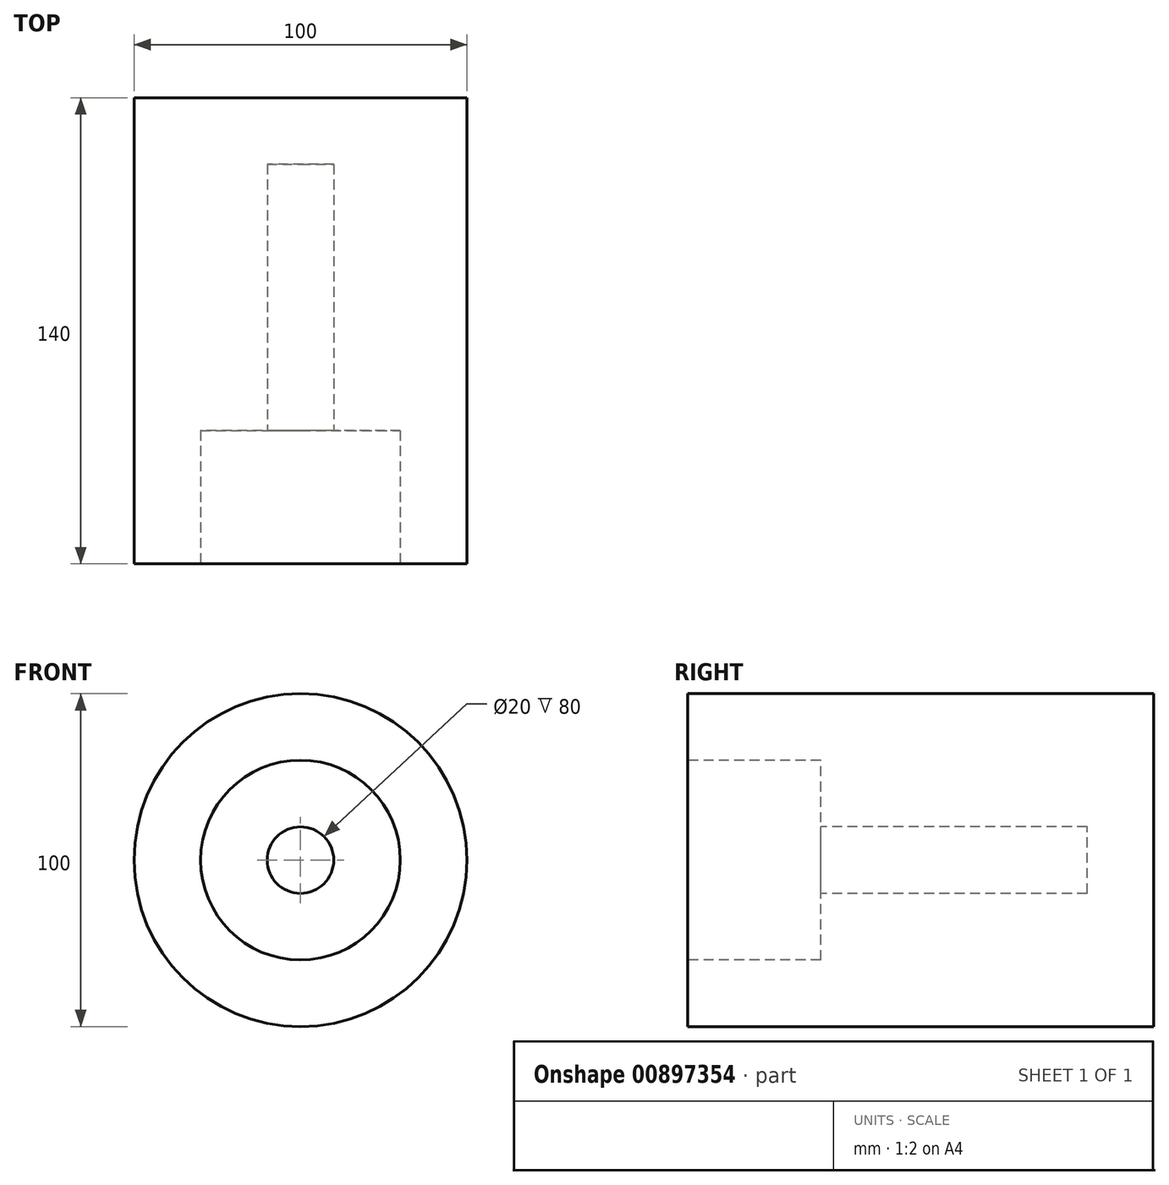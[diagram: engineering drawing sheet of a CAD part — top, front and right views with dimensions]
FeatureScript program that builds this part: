
annotation { "Feature Type Name" : "Feature", "Feature Type Description" : "" }
export const myFeature = defineFeature(function(context is Context, id is Id, definition is map)
    precondition{}
    {
        {
            var Q0;
            Q0=qCreatedBy(makeId("Front.planeOp"),FACE);
            var sketch = newSketch(context, id + "F0", { "sketchPlane" : qUnion([Q0])});
            skCircle(sketch, "E0", {"center": v(0, 0) * mm, "radius": 50 * mm});
            skSolve(sketch);
        }
        {
            var Q0;
            Q0=makeQuery(id+"F0.imprint","IMPRINT",FACE,{"disambiguationData":[TD([[makeQuery(id+"F0.imprint","IMPRINT",EDGE,{"derivedFrom":sQuery(id+"F0.wireOp",EDGE,"E0")}),1.0]])]});
            extrude(context, id + "F1", {"entities" : qUnion([Q0]), "depth" : 70 * mm, "offsetDistance" : 25.4 * mm});
        }
        {
            var Q0;
            Q0=makeQuery(id+"F1.opExtrude","CAP_FACE",FACE,{"disambiguationData":[OSD([sQuery(id+"F0.wireOp",EDGE,"E0")])],"isStart":true});
            extrude(context, id + "F2", {"entities" : qUnion([Q0]), "operationType" : NewBodyOperationType.ADD, "depth" : 70 * mm, "offsetDistance" : 25.4 * mm});
        }
        {
            var Q0;
            Q0=makeQuery(id+"F1.opExtrude","CAP_FACE",FACE,{"disambiguationData":[OSD([sQuery(id+"F0.wireOp",EDGE,"E0")])],"isStart":false});
            var sketch = newSketch(context, id + "F3", { "sketchPlane" : qUnion([Q0])});
            skCircle(sketch, "E1", {"center": v(0, 0) * mm, "radius": 30 * mm});
            skSolve(sketch);
        }
        {
            var Q0;
            Q0=makeQuery(id+"F3.imprint","IMPRINT",FACE,{"disambiguationData":[TD([[makeQuery(id+"F3.imprint","IMPRINT",EDGE,{"derivedFrom":sQuery(id+"F3.wireOp",EDGE,"E1")}),1.0]])]});
            extrude(context, id + "F4", {"entities" : qUnion([Q0]), "operationType" : NewBodyOperationType.REMOVE, "oppositeDirection" : true, "depth" : 40 * mm, "offsetDistance" : 25.4 * mm});
        }
        {
            var Q0;
            Q0=makeQuery(id+"F4.boolean.opBoolean","COPY",FACE,{"derivedFrom":makeQuery(id+"F4.opExtrude","CAP_FACE",FACE,{"disambiguationData":[OSD([sQuery(id+"F3.wireOp",EDGE,"E1")])],"isStart":false})});
            var sketch = newSketch(context, id + "F5", { "sketchPlane" : qUnion([Q0])});
            skCircle(sketch, "E2", {"center": v(0, 0) * mm, "radius": 10 * mm});
            skSolve(sketch);
        }
        {
            var Q0;
            Q0 = qSketchRegion(id + "F5", true);
            extrude(context, id + "F6", {"entities" : qUnion([Q0]), "operationType" : NewBodyOperationType.REMOVE, "oppositeDirection" : true, "depth" : 80 * mm, "offsetDistance" : 25.4 * mm});
        }
    });
